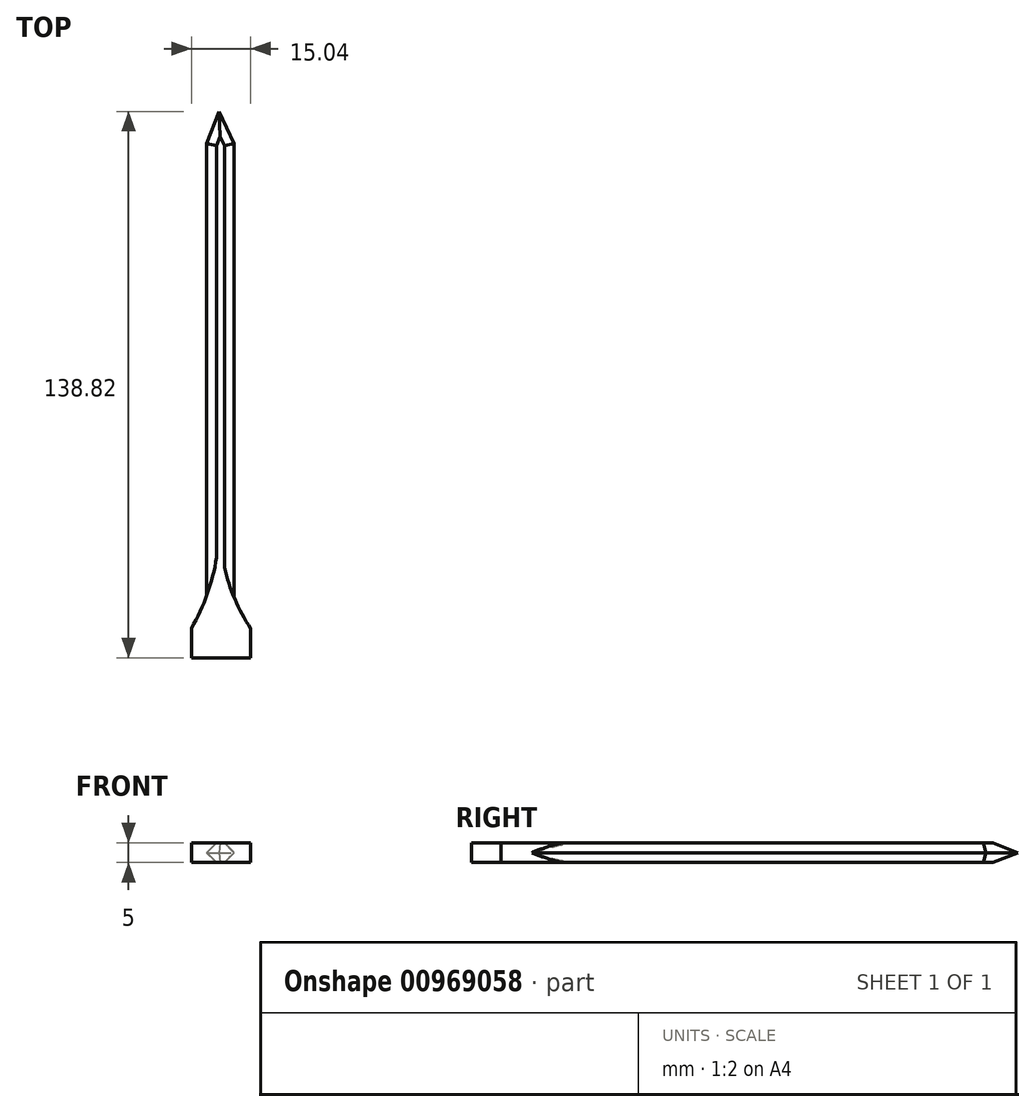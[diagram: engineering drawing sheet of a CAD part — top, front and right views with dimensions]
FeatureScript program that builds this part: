
annotation { "Feature Type Name" : "Feature", "Feature Type Description" : "" }
export const myFeature = defineFeature(function(context is Context, id is Id, definition is map)
    precondition{}
    {
        {
            var Q0;
            Q0=qCreatedBy(makeId("Top.planeOp"),FACE);
            var sketch = newSketch(context, id + "F0", { "sketchPlane" : qUnion([Q0])});
            skLineSegment(sketch, "E0.top", {"start": v(-3.18, -76.22) * mm, "end": v(3.79, -76.22) * mm});
            skLineSegment(sketch, "E0.left", {"start": v(-3.18, 54.1) * mm, "end": v(-3.18, -76.22) * mm});
            skLineSegment(sketch, "E0.right", {"start": v(3.79, 54.1) * mm, "end": v(3.79, -76.22) * mm});
            skLineSegment(sketch, "E1", {"start": v(-3.18, 54.1) * mm, "end": v(0, 62.28) * mm});
            skLineSegment(sketch, "E2", {"start": v(0, 62.28) * mm, "end": v(3.79, 54.1) * mm});
            skLineSegment(sketch, "E3", {"start": v(3.79, -76.22) * mm, "end": v(3.79, 54.1) * mm});
            skSolve(sketch);
        }
        {
            var Q0;
            Q0 = qSketchRegion(id + "F0", true);
            extrude(context, id + "F1", {"entities" : qUnion([Q0]), "endBound" : BoundingType.SYMMETRIC, "depth" : 5 * mm, "offsetDistance" : 25 * mm});
        }
        {
            var Q0;
            Q0=makeQuery(id+"F1.opExtrude","CAP_FACE",FACE,{"disambiguationData":[OSD([sQuery(id+"F0.wireOp",EDGE,"E1"),sQuery(id+"F0.wireOp",EDGE,"E2"),sQuery(id+"F0.wireOp",EDGE,"E0.left"),sQuery(id+"F0.wireOp",EDGE,"E0.top"),sQuery(id+"F0.wireOp",EDGE,"E3")])],"isStart":true});
            var Q1;
            Q1=makeQuery(id+"F1.opExtrude","CAP_FACE",FACE,{"disambiguationData":[OSD([sQuery(id+"F0.wireOp",EDGE,"E1"),sQuery(id+"F0.wireOp",EDGE,"E2"),sQuery(id+"F0.wireOp",EDGE,"E0.left"),sQuery(id+"F0.wireOp",EDGE,"E0.top"),sQuery(id+"F0.wireOp",EDGE,"E3")])],"isStart":false});
            chamfer(context, id + "F2", {"entities" : qUnion([Q0, Q1]), "width" : 2.5 * mm, "tangentPropagation" : true});
        }
        {
            var Q0;
            Q0=qCreatedBy(makeId("Top.planeOp"),FACE);
            var sketch = newSketch(context, id + "F3", { "sketchPlane" : qUnion([Q0])});
            skLineSegment(sketch, "E4.top", {"start": v(-7.07, -76.54) * mm, "end": v(7.97, -76.54) * mm});
            skLineSegment(sketch, "E4.left", {"start": v(-7.07, -69.03) * mm, "end": v(-7.07, -76.54) * mm});
            skLineSegment(sketch, "E4.right", {"start": v(7.97, -69.03) * mm, "end": v(7.97, -76.54) * mm});
            skArc(sketch, "E5", {"start": v(0, -42.56) * mm, "mid": v(2.04, -56.38) * mm, "end": v(7.97, -69.03) * mm});
            skArc(sketch, "E6", {"start": v(-7.07, -69.03) * mm, "mid": v(-1.8, -56.26) * mm, "end": v(0, -42.56) * mm});
            skSolve(sketch);
        }
        {
            var Q0;
            Q0 = qSketchRegion(id + "F3", true);
            extrude(context, id + "F4", {"entities" : qUnion([Q0]), "operationType" : NewBodyOperationType.ADD, "endBound" : BoundingType.SYMMETRIC, "depth" : 5 * mm, "offsetDistance" : 25 * mm});
        }
    });
